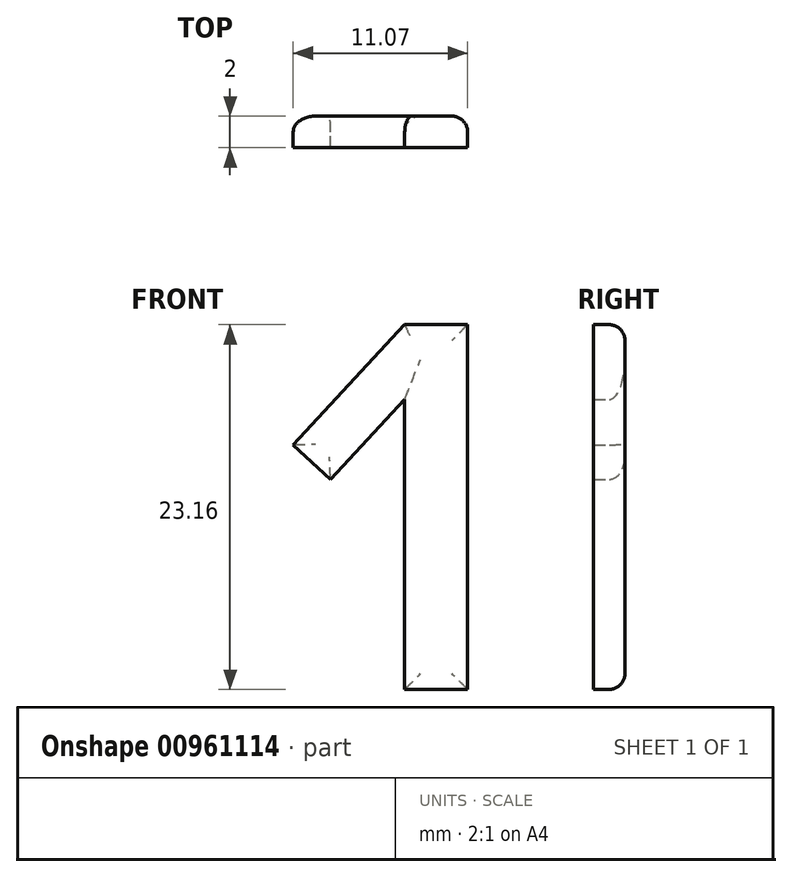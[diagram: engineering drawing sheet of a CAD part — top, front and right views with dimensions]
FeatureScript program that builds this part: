
annotation { "Feature Type Name" : "Feature", "Feature Type Description" : "" }
export const myFeature = defineFeature(function(context is Context, id is Id, definition is map)
    precondition{}
    {
        {
            var Q0;
            Q0=qCreatedBy(makeId("Front.planeOp"),FACE);
            var sketch = newSketch(context, id + "F0", { "sketchPlane" : qUnion([Q0])});
            skLineSegment(sketch, "E0", {"start": v(-36.02, 0) * mm, "end": v(-36.02, 18.42) * mm});
            skLineSegment(sketch, "E1", {"start": v(-36.02, 18.42) * mm, "end": v(-40.74, 13.34) * mm});
            skLineSegment(sketch, "E2", {"start": v(-40.74, 13.34) * mm, "end": v(-43.1, 15.53) * mm});
            skLineSegment(sketch, "E3", {"start": v(-43.1, 15.53) * mm, "end": v(-36.02, 23.16) * mm});
            skLineSegment(sketch, "E4", {"start": v(-36.02, 23.16) * mm, "end": v(-32.03, 23.16) * mm});
            skLineSegment(sketch, "E5", {"start": v(-32.03, 23.16) * mm, "end": v(-32.03, 0) * mm});
            skLineSegment(sketch, "E6", {"start": v(-32.03, 0) * mm, "end": v(-36.02, 0) * mm});
            skSolve(sketch);
        }
        {
            var Q0;
            Q0=makeQuery(id+"F0.imprint","IMPRINT",FACE,{"disambiguationData":[TD([[makeQuery(id+"F0.imprint","IMPRINT",EDGE,{"derivedFrom":sQuery(id+"F0.wireOp",EDGE,"E0")}),-1.0]])]});
            extrude(context, id + "F1", {"entities" : qUnion([Q0]), "depth" : 2 * mm, "offsetDistance" : 25 * mm});
        }
        {
            var Q0;
            Q0=makeQuery(id+"F1.opExtrude","CAP_EDGE",EDGE,{"disambiguationData":[OSD([sQuery(id+"F0.wireOp",EDGE,"E0")])],"isStart":true});
            var Q1;
            Q1=makeQuery(id+"F1.opExtrude","CAP_FACE",FACE,{"disambiguationData":[OSD([sQuery(id+"F0.wireOp",EDGE,"E0"),sQuery(id+"F0.wireOp",EDGE,"E1"),sQuery(id+"F0.wireOp",EDGE,"E2"),sQuery(id+"F0.wireOp",EDGE,"E3"),sQuery(id+"F0.wireOp",EDGE,"E4"),sQuery(id+"F0.wireOp",EDGE,"E5"),sQuery(id+"F0.wireOp",EDGE,"E6")])],"isStart":true});
            fillet(context, id + "F2", {"entities" : qUnion([Q0, Q1]), "radius" : 1 * mm, "tangentPropagation" : true, "allowEdgeOverflow" : false});
        }
    });
